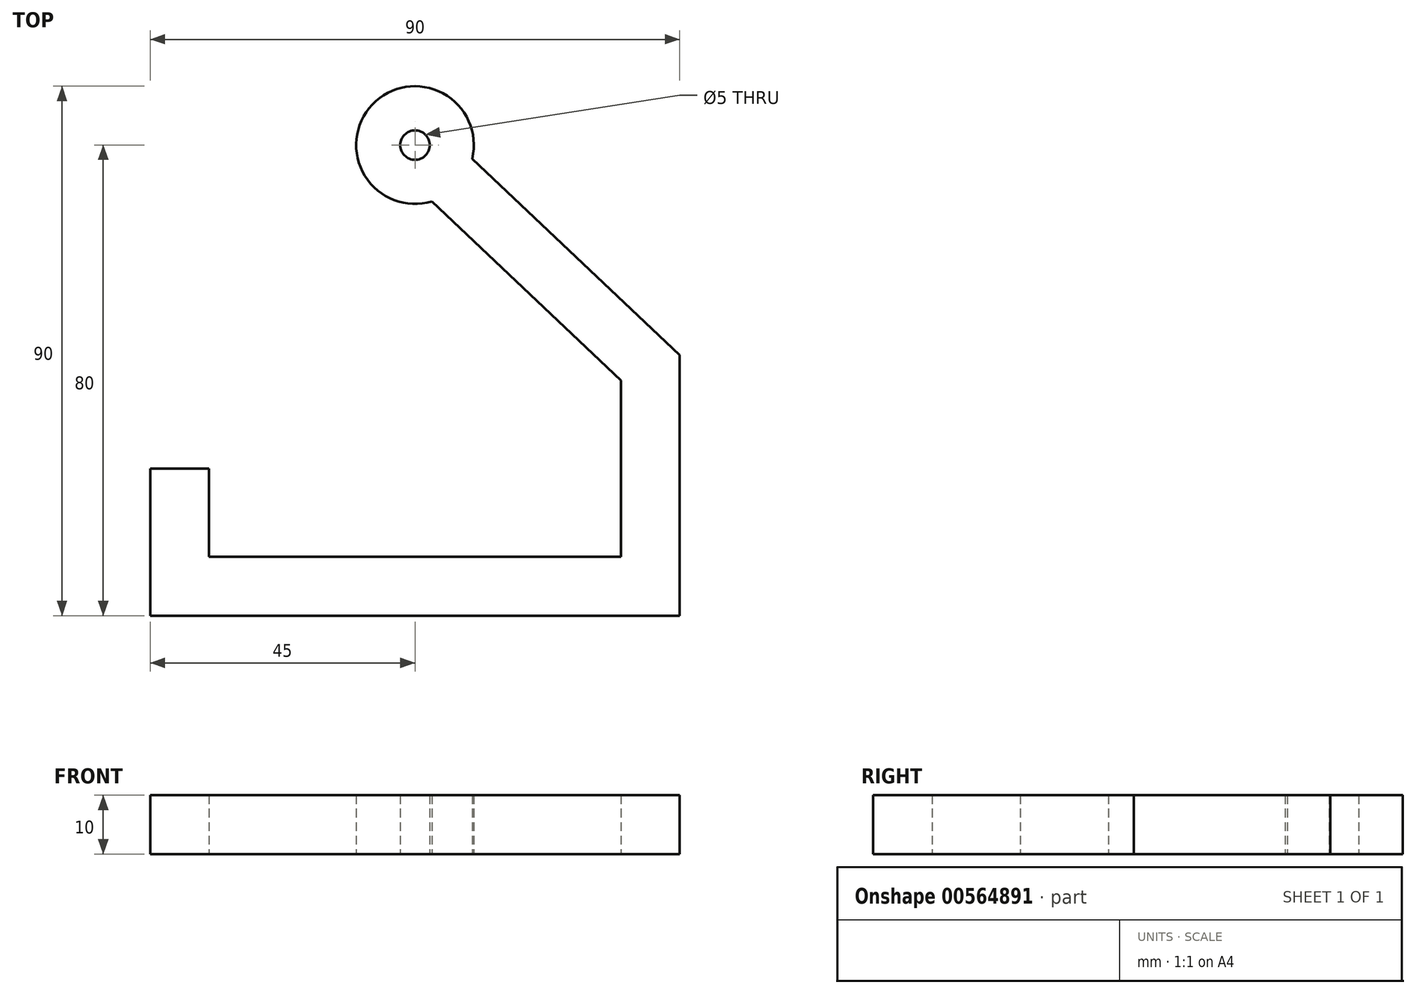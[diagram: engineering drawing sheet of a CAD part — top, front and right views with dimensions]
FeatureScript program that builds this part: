
annotation { "Feature Type Name" : "Feature", "Feature Type Description" : "" }
export const myFeature = defineFeature(function(context is Context, id is Id, definition is map)
    precondition{}
    {
        {
            var Q0;
            Q0=qCreatedBy(makeId("Top.planeOp"),FACE);
            var sketch = newSketch(context, id + "F0", { "sketchPlane" : qUnion([Q0])});
            skPoint(sketch, "E0", {"position": v(0, 40) * mm});
            skPoint(sketch, "E1", {"position": v(0, -40) * mm});
            skCircle(sketch, "E2", {"center": v(0, 40) * mm, "radius": 2.5 * mm});
            skLineSegment(sketch, "E3", {"start": v(0, -40) * mm, "end": v(-45, -40) * mm});
            skLineSegment(sketch, "E4", {"start": v(-45, -40) * mm, "end": v(-45, -15) * mm});
            skLineSegment(sketch, "E5", {"start": v(35, -30) * mm, "end": v(35, 0) * mm});
            skLineSegment(sketch, "E6", {"start": v(0, -40) * mm, "end": v(45, -40) * mm});
            skLineSegment(sketch, "E7", {"start": v(45, -40) * mm, "end": v(45, 0) * mm});
            skLineSegment(sketch, "E8", {"start": v(-45, -15) * mm, "end": v(-35, -15) * mm});
            skLineSegment(sketch, "E9", {"start": v(-35, -15) * mm, "end": v(-35, -30) * mm});
            skLineSegment(sketch, "E10", {"start": v(-35, -30) * mm, "end": v(35, -30) * mm});
            skPoint(sketch, "E11", {"position": v(2.85, 30.42) * mm});
            skPoint(sketch, "E12", {"position": v(9.73, 37.68) * mm});
            skLineSegment(sketch, "E13", {"start": v(35, 0) * mm, "end": v(2.85, 30.42) * mm});
            skLineSegment(sketch, "E14", {"start": v(9.73, 37.68) * mm, "end": v(45, 4.3) * mm});
            skLineSegment(sketch, "E15", {"start": v(45, 0) * mm, "end": v(45, 4.3) * mm});
            skArc(sketch, "E16", {"start": v(9.73, 37.68) * mm, "mid": v(-7.26, 46.87) * mm, "end": v(2.85, 30.42) * mm});
            skSolve(sketch);
        }
        {
            var Q0;
            Q0=makeQuery(id+"F0.imprint","IMPRINT",FACE,{"disambiguationData":[TD([[makeQuery(id+"F0.imprint","IMPRINT",EDGE,{"derivedFrom":sQuery(id+"F0.wireOp",EDGE,"E2")}),-1.0]])]});
            extrude(context, id + "F1", {"entities" : qUnion([Q0]), "depth" : 10 * mm, "offsetDistance" : 25 * mm});
        }
    });
